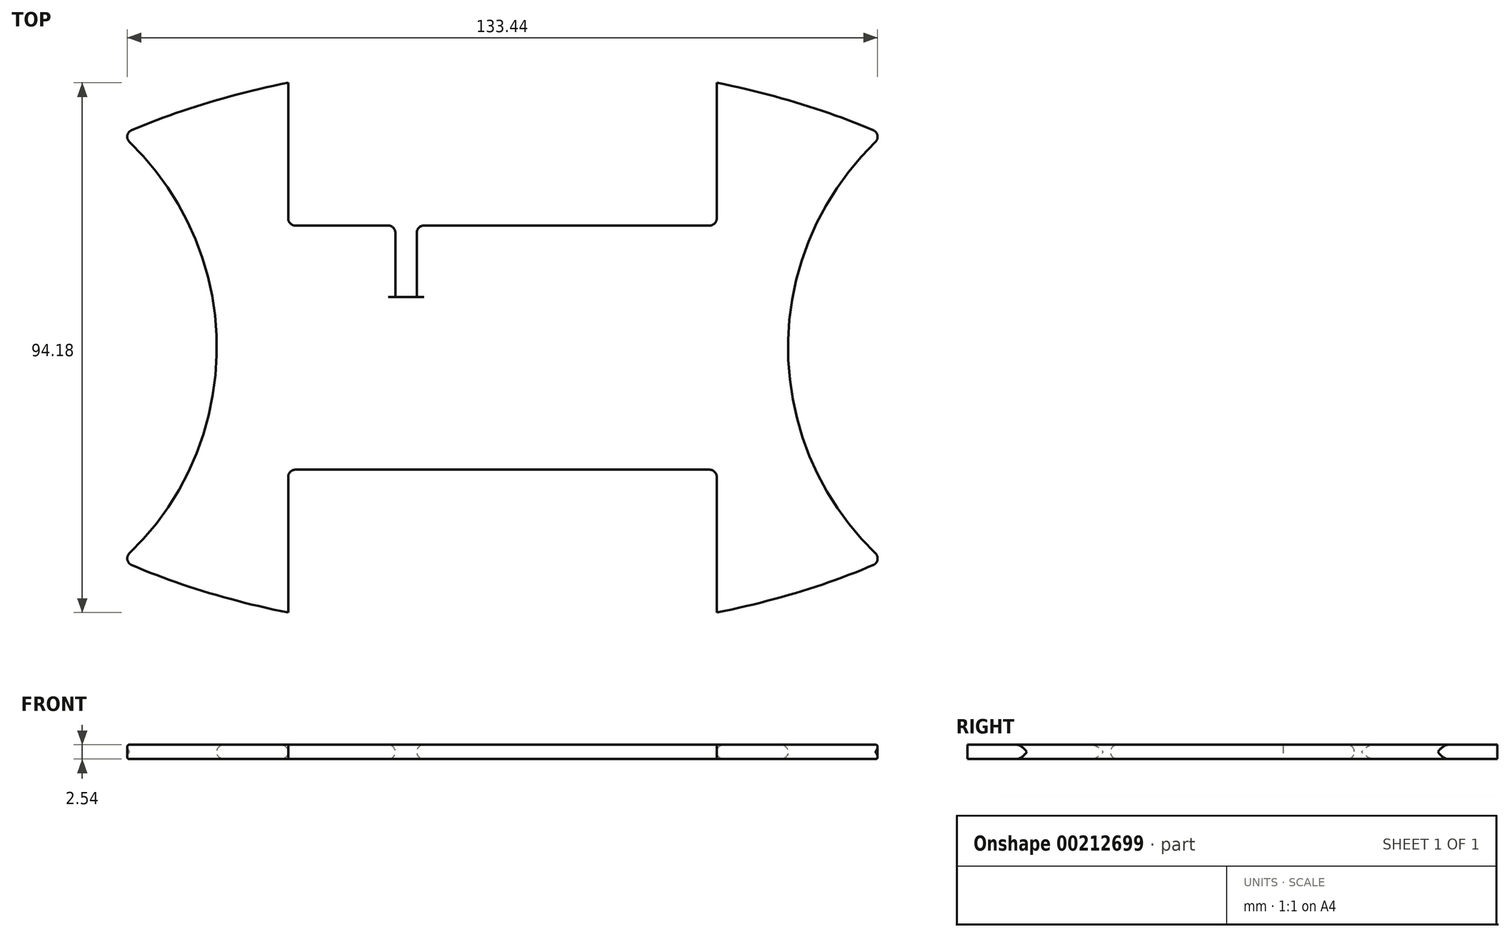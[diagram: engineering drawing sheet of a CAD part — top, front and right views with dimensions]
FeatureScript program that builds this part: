
annotation { "Feature Type Name" : "Feature", "Feature Type Description" : "" }
export const myFeature = defineFeature(function(context is Context, id is Id, definition is map)
    precondition{}
    {
        {
            var Q0;
            Q0=qCreatedBy(makeId("Top.planeOp"),FACE);
            var sketch = newSketch(context, id + "F0", { "sketchPlane" : qUnion([Q0])});
            skEllipticalArc(sketch, "E0", {});
            skArc(sketch, "E1", {"start": v(67.73, 37.86) * mm, "mid": v(55.23, 20.74) * mm, "end": v(50.8, 0) * mm});
            skLineSegment(sketch, "E2", {"start": v(-101.6, 0) * mm, "end": v(101.6, 0) * mm, "construction": true});
            skPoint(sketch, "E2.endSnap0", {"position": v(-101.6, 0) * mm});
            skLineSegment(sketch, "E3", {"start": v(0, 0) * mm, "end": v(0, 59.74) * mm, "construction": true});
            skArc(sketch, "E4.MirrorCS", {"start": v(67.73, -37.86) * mm, "mid": v(55.23, -20.74) * mm, "end": v(50.8, 0) * mm});
            skArc(sketch, "E5.MirrorCS", {"start": v(-67.73, 37.86) * mm, "mid": v(-55.23, 20.74) * mm, "end": v(-50.8, 0) * mm});
            skArc(sketch, "E6.MirrorCS", {"start": v(-67.73, -37.86) * mm, "mid": v(-55.23, -20.74) * mm, "end": v(-50.8, 0) * mm});
            skEllipticalArc(sketch, "E7.trimOffspring", {});
            skLineSegment(sketch, "E8.top", {"start": v(-38.1, 21.7) * mm, "end": v(38.1, 21.7) * mm});
            skLineSegment(sketch, "E8.left", {"start": v(-38.1, 47.1) * mm, "end": v(-38.1, 21.7) * mm});
            skLineSegment(sketch, "E8.right", {"start": v(38.1, 47.1) * mm, "end": v(38.1, 21.7) * mm});
            skEllipticalArc(sketch, "E9.trimOffspring", {});
            skLineSegment(sketch, "E10.MirrorCS", {"start": v(-38.1, -21.7) * mm, "end": v(38.1, -21.7) * mm});
            skLineSegment(sketch, "E11.MirrorCS", {"start": v(38.1, -47.1) * mm, "end": v(38.1, -21.7) * mm});
            skLineSegment(sketch, "E12.MirrorCS", {"start": v(-38.1, -47.1) * mm, "end": v(-38.1, -21.7) * mm});
            skEllipticalArc(sketch, "E13.trimOffspring", {});
            skLineSegment(sketch, "E14.bottom", {"start": v(-19.05, 21.7) * mm, "end": v(-15.24, 21.7) * mm});
            skLineSegment(sketch, "E14.top", {"start": v(-19.05, 9) * mm, "end": v(-15.24, 9) * mm});
            skLineSegment(sketch, "E14.left", {"start": v(-19.05, 21.7) * mm, "end": v(-19.05, 9) * mm});
            skLineSegment(sketch, "E14.right", {"start": v(-15.24, 21.7) * mm, "end": v(-15.24, 9) * mm});
            const initialGuessF0  = {"E0": [0, 0, 1, 0, 0.1016, 0.0508, 3.982661324157723, 4.327992205889053], "E7.trimOffspring": [0, 0, 1, 0, 0.1016, 0.0508, 0.8410686705679303, 1.1863995522992605], "E9.trimOffspring": [0, 0, 1, 0, 0.1016, 0.0508, 1.9551931012905328, 2.300523983021863], "E13.trimOffspring": [0, 0, 1, 0, 0.1016, 0.0508, 5.096785754880326, 5.442116636611656]};
            skSetInitialGuess(sketch, initialGuessF0);
            skSolve(sketch);
        }
        {
            var Q0;
            Q0=makeQuery(id+"F0.imprint","IMPRINT",FACE,{"disambiguationData":[TD([[makeQuery(id+"F0.imprint","IMPRINT",EDGE,{"derivedFrom":sQuery(id+"F0.wireOp",EDGE,"E0")}),1.0]])]});
            extrude(context, id + "F1", {"entities" : qUnion([Q0]), "depth" : 2.54 * mm});
        }
        {
            var Q0;
            Q0=makeQuery(id+"F1.opExtrude","SWEPT_FACE",FACE,{"disambiguationData":[OSD([sQuery(id+"F0.wireOp",EDGE,"E1"),sQuery(id+"F0.wireOp",EDGE,"E4.MirrorCS")])]});
            var Q1;
            Q1=makeQuery(id+"F1.opExtrude","SWEPT_FACE",FACE,{"disambiguationData":[OSD([sQuery(id+"F0.wireOp",EDGE,"E10.MirrorCS")])]});
            var Q2;
            Q2=makeQuery(id+"F1.opExtrude","SWEPT_FACE",FACE,{"disambiguationData":[OSD([sQuery(id+"F0.wireOp",EDGE,"E5.MirrorCS"),sQuery(id+"F0.wireOp",EDGE,"E6.MirrorCS")])]});
            var Q3;
            {var subQ0=sQuery(id+"F0.wireOp",EDGE,"E8.top");Q3=makeQuery(id+"F1.opExtrude","SWEPT_FACE",FACE,{"disambiguationData":[OSD([subQ0]),TDD([makeQuery(id+"F0.imprint","IMPRINT",EDGE,{"disambiguationData":[TD([[makeQuery(id+"F0.imprint","INTERSECT",VERTEX,{"derivedFrom":[subQ0,sQuery(id+"F0.wireOp",EDGE,"E8.right")]}),1.0]])],"derivedFrom":subQ0})])]});}
            var Q4;
            {var subQ0=sQuery(id+"F0.wireOp",EDGE,"E8.top");Q4=makeQuery(id+"F1.opExtrude","SWEPT_FACE",FACE,{"disambiguationData":[OSD([subQ0]),TDD([makeQuery(id+"F0.imprint","IMPRINT",EDGE,{"disambiguationData":[TD([[makeQuery(id+"F0.imprint","INTERSECT",VERTEX,{"derivedFrom":[subQ0,sQuery(id+"F0.wireOp",EDGE,"E8.left")]}),-1.0]])],"derivedFrom":subQ0})])]});}
            var Q5;
            Q5=makeQuery(id+"F1.opExtrude","CAP_EDGE",EDGE,{"disambiguationData":[OSD([sQuery(id+"F0.wireOp",EDGE,"E14.right")])],"isStart":false});
            var Q6;
            Q6=makeQuery(id+"F1.opExtrude","CAP_EDGE",EDGE,{"disambiguationData":[OSD([sQuery(id+"F0.wireOp",EDGE,"E14.left")])],"isStart":false});
            var Q7;
            Q7=makeQuery(id+"F1.opExtrude","CAP_EDGE",EDGE,{"disambiguationData":[OSD([sQuery(id+"F0.wireOp",EDGE,"E14.right")])],"isStart":true});
            var Q8;
            Q8=makeQuery(id+"F1.opExtrude","CAP_EDGE",EDGE,{"disambiguationData":[OSD([sQuery(id+"F0.wireOp",EDGE,"E14.left")])],"isStart":true});
            fillet(context, id + "F2", {"entities" : qUnion([Q0, Q1, Q2, Q3, Q4, Q5, Q6, Q7, Q8]), "radius" : 1.27 * mm, "tangentPropagation" : true, "allowEdgeOverflow" : false});
        }
    });
